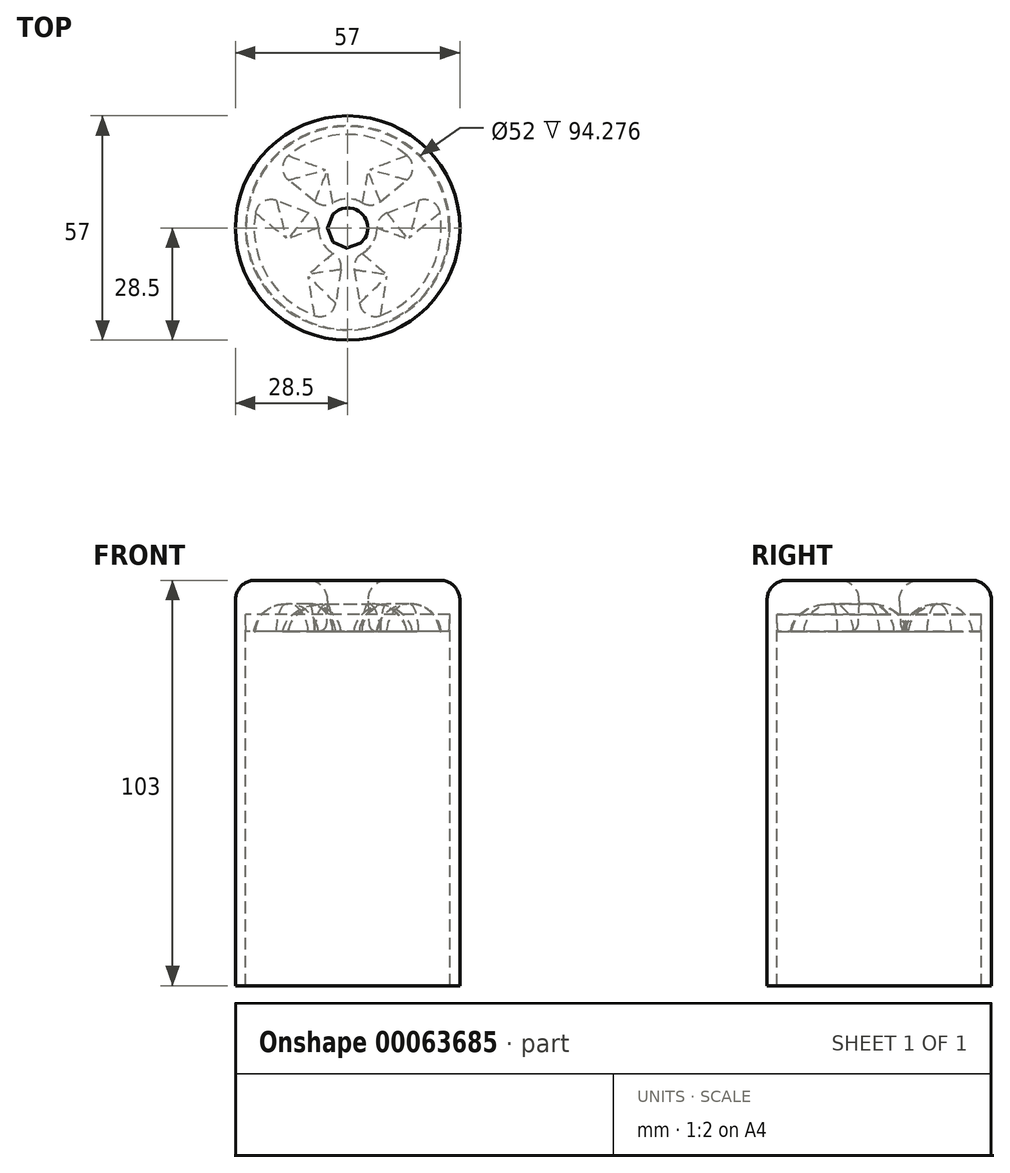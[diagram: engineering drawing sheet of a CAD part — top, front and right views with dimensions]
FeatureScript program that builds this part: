
annotation { "Feature Type Name" : "Feature", "Feature Type Description" : "" }
export const myFeature = defineFeature(function(context is Context, id is Id, definition is map)
    precondition{}
    {
        {
            var Q0;
            Q0=qCreatedBy(makeId("Top.planeOp"),FACE);
            var sketch = newSketch(context, id + "F0", { "sketchPlane" : qUnion([Q0])});
            skCircle(sketch, "E0", {"center": v(0, 0) * mm, "radius": 28.5 * mm});
            skCircle(sketch, "E1", {"center": v(0, 0) * mm, "radius": 26 * mm});
            skSolve(sketch);
        }
        {
            var Q0;
            Q0 = qSketchRegion(id + "F0", true);
            extrude(context, id + "F1", {"entities" : qUnion([Q0]), "oppositeDirection" : true, "depth" : 100 * mm});
        }
        {
            var Q0;
            Q0=qCreatedBy(makeId("Top.planeOp"),FACE);
            var sketch = newSketch(context, id + "F2", { "sketchPlane" : qUnion([Q0])});
            skCircle(sketch, "E2", {"center": v(0, 0) * mm, "radius": 28.5 * mm});
            skCircle(sketch, "E3", {"center": v(0, 0) * mm, "radius": 26.3 * mm});
            skCircle(sketch, "E4", {"center": v(0, 0) * mm, "radius": 5 * mm});
            skSolve(sketch);
        }
        {
            var Q0;
            Q0=makeQuery(id+"F2.imprint","IMPRINT",FACE,{"disambiguationData":[TD([[makeQuery(id+"F2.imprint","IMPRINT",EDGE,{"derivedFrom":sQuery(id+"F2.wireOp",EDGE,"E3")}),1.0]])]});
            var Q1;
            Q1=makeQuery(id+"F2.imprint","IMPRINT",FACE,{"disambiguationData":[TD([[makeQuery(id+"F2.imprint","IMPRINT",EDGE,{"derivedFrom":sQuery(id+"F2.wireOp",EDGE,"E2")}),1.0]])]});
            extrude(context, id + "F3", {"entities" : qUnion([Q0, Q1]), "depth" : 3 * mm});
        }
        {
            var Q0;
            Q0=makeQuery(id+"F2.imprint","IMPRINT",FACE,{"disambiguationData":[TD([[makeQuery(id+"F2.imprint","IMPRINT",EDGE,{"derivedFrom":sQuery(id+"F2.wireOp",EDGE,"E3")}),1.0]])]});
            extrude(context, id + "F4", {"entities" : qUnion([Q0]), "operationType" : NewBodyOperationType.ADD, "oppositeDirection" : true, "depth" : 10 * mm, "hasDraft" : true, "draftAngle" : 3 * degree, "draftPullDirection" : true});
        }
        {
            var Q0;
            Q0=makeQuery(id+"F4.opExtrude","CAP_EDGE",EDGE,{"disambiguationData":[OSD([sQuery(id+"F2.wireOp",EDGE,"E4")])],"isStart":false});
            fillet(context, id + "F5", {"entities" : qUnion([Q0]), "radius" : 2 * mm, "tangentPropagation" : true, "allowEdgeOverflow" : false});
        }
        {
            var Q0;
            Q0=makeQuery(id+"F3.opExtrude","CAP_EDGE",EDGE,{"disambiguationData":[OSD([sQuery(id+"F2.wireOp",EDGE,"E2")])],"isStart":false});
            var Q1;
            Q1=makeQuery(id+"F3.opExtrude","CAP_EDGE",EDGE,{"disambiguationData":[OSD([sQuery(id+"F2.wireOp",EDGE,"E4")])],"isStart":false});
            fillet(context, id + "F6", {"entities" : qUnion([Q0, Q1]), "radius" : 5 * mm, "tangentPropagation" : true, "allowEdgeOverflow" : false});
        }
        {
            var Q0;
            Q0=makeQuery(id+"F4.opExtrude","CAP_FACE",FACE,{"disambiguationData":[OSD([sQuery(id+"F2.wireOp",EDGE,"E3"),sQuery(id+"F2.wireOp",EDGE,"E4")])],"isStart":false});
            var sketch = newSketch(context, id + "F7", { "sketchPlane" : qUnion([Q0])});
            skArc(sketch, "E5", {"start": v(-8.4, 22.24) * mm, "mid": v(-20.59, 11.89) * mm, "end": v(-23.46, -3.85) * mm});
            skLineSegment(sketch, "E6", {"start": v(0, 0) * mm, "end": v(0, 23.77) * mm, "construction": true});
            skLineSegment(sketch, "E7", {"start": v(-1.67, 10.57) * mm, "end": v(-3.03, 19.13) * mm});
            skArc(sketch, "E8", {"start": v(-3.65, 6.46) * mm, "mid": v(-6.43, 3.71) * mm, "end": v(-7.42, -0.06) * mm});
            skPoint(sketch, "E9.visualSharp", {"position": v(-3.72, 23.48) * mm});
            skArc(sketch, "E9.filletArc", {"start": v(-3.03, 19.13) * mm, "mid": v(-4.97, 21.96) * mm, "end": v(-8.4, 22.24) * mm});
            skPoint(sketch, "E10.visualSharp", {"position": v(-1.18, 7.43) * mm});
            skArc(sketch, "E10.filletArc", {"start": v(-3.65, 6.46) * mm, "mid": v(-2.02, 8.2) * mm, "end": v(-1.67, 10.57) * mm});
            skArc(sketch, "E11.MirrorCS", {"start": v(3.03, 19.13) * mm, "mid": v(4.97, 21.96) * mm, "end": v(8.4, 22.24) * mm});
            skLineSegment(sketch, "E12.MirrorCS", {"start": v(1.67, 10.57) * mm, "end": v(3.03, 19.13) * mm});
            skArc(sketch, "E13.MirrorCS", {"start": v(3.65, 6.46) * mm, "mid": v(2.02, 8.2) * mm, "end": v(1.67, 10.57) * mm});
            skLineSegment(sketch, "E14.1.0", {"start": v(-9.99, -3.83) * mm, "end": v(-18.08, -6.94) * mm});
            skArc(sketch, "E14.1.2", {"start": v(-7.42, -0.06) * mm, "mid": v(-8.12, -2.35) * mm, "end": v(-9.99, -3.83) * mm});
            skArc(sketch, "E14.1.3", {"start": v(-15.05, -12.19) * mm, "mid": v(-16.53, -15.28) * mm, "end": v(-15.07, -18.39) * mm});
            skArc(sketch, "E14.1.4", {"start": v(-3.77, -6.4) * mm, "mid": v(-6.1, -5.85) * mm, "end": v(-8.31, -6.73) * mm});
            skArc(sketch, "E14.1.6", {"start": v(-18.08, -6.94) * mm, "mid": v(-21.5, -6.68) * mm, "end": v(-23.46, -3.85) * mm});
            skLineSegment(sketch, "E14.1.7", {"start": v(-8.31, -6.73) * mm, "end": v(-15.05, -12.19) * mm});
            skLineSegment(sketch, "E14.2.0", {"start": v(8.31, -6.73) * mm, "end": v(15.05, -12.19) * mm});
            skArc(sketch, "E14.2.2", {"start": v(3.77, -6.4) * mm, "mid": v(6.1, -5.85) * mm, "end": v(8.31, -6.73) * mm});
            skArc(sketch, "E14.2.3", {"start": v(18.08, -6.94) * mm, "mid": v(21.5, -6.68) * mm, "end": v(23.46, -3.85) * mm});
            skArc(sketch, "E14.2.4", {"start": v(7.42, -0.06) * mm, "mid": v(8.12, -2.35) * mm, "end": v(9.99, -3.83) * mm});
            skArc(sketch, "E14.2.6", {"start": v(15.05, -12.19) * mm, "mid": v(16.53, -15.28) * mm, "end": v(15.07, -18.39) * mm});
            skLineSegment(sketch, "E14.2.7", {"start": v(9.99, -3.83) * mm, "end": v(18.08, -6.94) * mm});
            skCircle(sketch, "E15", {"center": v(0, 0) * mm, "radius": 6.98 * mm, "construction": true});
            skArc(sketch, "E16.trimOffspring", {"start": v(-3.77, -6.4) * mm, "mid": v(0, -7.42) * mm, "end": v(3.77, -6.4) * mm});
            skArc(sketch, "E17.trimOffspring", {"start": v(7.42, -0.06) * mm, "mid": v(6.43, 3.71) * mm, "end": v(3.65, 6.46) * mm});
            skArc(sketch, "E18.trimOffspring", {"start": v(23.46, -3.85) * mm, "mid": v(20.59, 11.89) * mm, "end": v(8.4, 22.24) * mm});
            skArc(sketch, "E19.trimOffspring", {"start": v(-15.07, -18.39) * mm, "mid": v(0, -23.77) * mm, "end": v(15.07, -18.39) * mm});
            skSolve(sketch);
        }
        {
            var Q0;
            Q0 = qSketchRegion(id + "F7", true);
            var Q1;
            Q1=sQuery(id+"F7.wireOp",EDGE,"E7");
            var Q2;
            Q2=sQuery(id+"F7.wireOp",EDGE,"E9.filletArc");
            var Q3;
            Q3=sQuery(id+"F7.wireOp",EDGE,"E10.filletArc");
            var Q4;
            Q4=sQuery(id+"F7.wireOp",EDGE,"E8");
            var Q5;
            Q5=sQuery(id+"F7.wireOp",EDGE,"E14.1.2");
            var Q6;
            Q6=sQuery(id+"F7.wireOp",EDGE,"E14.1.0");
            var Q7;
            Q7=sQuery(id+"F7.wireOp",EDGE,"E14.1.6");
            var Q8;
            Q8=sQuery(id+"F7.wireOp",EDGE,"E14.1.1");
            var Q9;
            Q9=sQuery(id+"F7.wireOp",EDGE,"E14.1.3");
            var Q10;
            Q10=sQuery(id+"F7.wireOp",EDGE,"E14.1.7");
            var Q11;
            Q11=sQuery(id+"F7.wireOp",EDGE,"E14.1.4");
            var Q12;
            Q12=sQuery(id+"F7.wireOp",EDGE,"E16.trimOffspring");
            var Q13;
            Q13=sQuery(id+"F7.wireOp",EDGE,"E14.2.2");
            var Q14;
            Q14=sQuery(id+"F7.wireOp",EDGE,"E14.2.0");
            var Q15;
            Q15=sQuery(id+"F7.wireOp",EDGE,"E14.2.6");
            var Q16;
            Q16=sQuery(id+"F7.wireOp",EDGE,"E14.2.1");
            var Q17;
            Q17=sQuery(id+"F7.wireOp",EDGE,"E14.2.3");
            var Q18;
            Q18=sQuery(id+"F7.wireOp",EDGE,"E14.2.7");
            var Q19;
            Q19=sQuery(id+"F7.wireOp",EDGE,"E14.2.4");
            var Q20;
            Q20=sQuery(id+"F7.wireOp",EDGE,"E17.trimOffspring");
            var Q21;
            Q21=sQuery(id+"F7.wireOp",EDGE,"E13.MirrorCS");
            var Q22;
            Q22=sQuery(id+"F7.wireOp",EDGE,"E12.MirrorCS");
            var Q23;
            Q23=sQuery(id+"F7.wireOp",EDGE,"E11.MirrorCS");
            var Q24;
            Q24=sQuery(id+"F7.wireOp",EDGE,"8f9500c2-0eae-47fa-844b-90024a585e13");
            extrude(context, id + "F8", {"entities" : qUnion([Q0]), "operationType" : NewBodyOperationType.REMOVE, "surfaceEntities" : qUnion([Q1, Q2, Q3, Q4, Q5, Q6, Q7, Q8, Q9, Q10, Q11, Q12, Q13, Q14, Q15, Q16, Q17, Q18, Q19, Q20, Q21, Q22, Q23, Q24]), "oppositeDirection" : true, "depth" : 7 * mm});
        }
        {
            var Q0;
            Q0=makeQuery(id+"F8.boolean.opBoolean","COPY",FACE,{"derivedFrom":makeQuery(id+"F8.opExtrude","CAP_FACE",FACE,{"disambiguationData":[OSD([sQuery(id+"F7.wireOp",EDGE,"E5"),sQuery(id+"F7.wireOp",EDGE,"E7"),sQuery(id+"F7.wireOp",EDGE,"E8"),sQuery(id+"F7.wireOp",EDGE,"E9.filletArc"),sQuery(id+"F7.wireOp",EDGE,"E10.filletArc"),sQuery(id+"F7.wireOp",EDGE,"E14.1.0"),sQuery(id+"F7.wireOp",EDGE,"E14.1.2"),sQuery(id+"F7.wireOp",EDGE,"E14.1.6")])],"isStart":false})});
            var Q1;
            Q1=makeQuery(id+"F8.boolean.opBoolean","COPY",FACE,{"derivedFrom":makeQuery(id+"F8.opExtrude","CAP_FACE",FACE,{"disambiguationData":[OSD([sQuery(id+"F7.wireOp",EDGE,"E11.MirrorCS"),sQuery(id+"F7.wireOp",EDGE,"E12.MirrorCS"),sQuery(id+"F7.wireOp",EDGE,"E13.MirrorCS"),sQuery(id+"F7.wireOp",EDGE,"E14.2.3"),sQuery(id+"F7.wireOp",EDGE,"E14.2.4"),sQuery(id+"F7.wireOp",EDGE,"E14.2.7"),sQuery(id+"F7.wireOp",EDGE,"E17.trimOffspring"),sQuery(id+"F7.wireOp",EDGE,"E18.trimOffspring")])],"isStart":false})});
            var Q2;
            Q2=makeQuery(id+"F8.boolean.opBoolean","COPY",FACE,{"derivedFrom":makeQuery(id+"F8.opExtrude","CAP_FACE",FACE,{"disambiguationData":[OSD([sQuery(id+"F7.wireOp",EDGE,"E14.1.3"),sQuery(id+"F7.wireOp",EDGE,"E14.1.4"),sQuery(id+"F7.wireOp",EDGE,"E14.1.7"),sQuery(id+"F7.wireOp",EDGE,"E14.2.0"),sQuery(id+"F7.wireOp",EDGE,"E14.2.2"),sQuery(id+"F7.wireOp",EDGE,"E14.2.6"),sQuery(id+"F7.wireOp",EDGE,"E16.trimOffspring"),sQuery(id+"F7.wireOp",EDGE,"E19.trimOffspring")])],"isStart":false})});
            fillet(context, id + "F9", {"entities" : qUnion([Q0, Q1, Q2]), "radius" : 8 * mm, "tangentPropagation" : true, "allowEdgeOverflow" : false});
        }
    });
